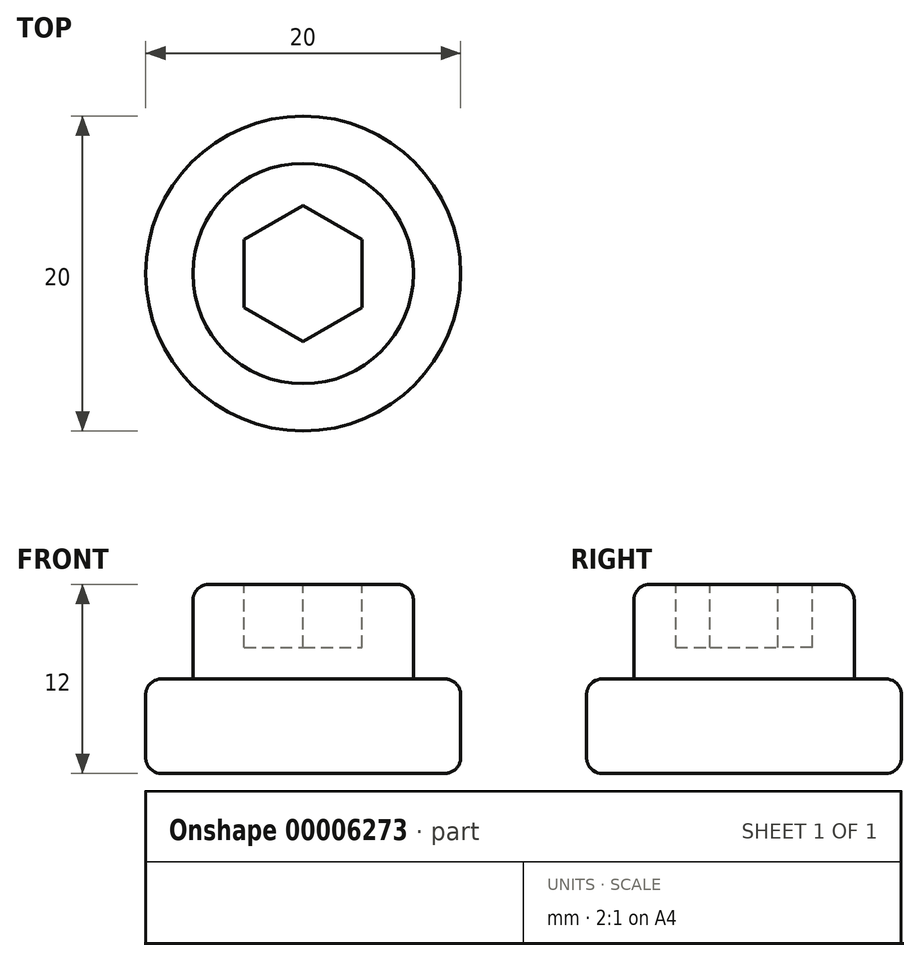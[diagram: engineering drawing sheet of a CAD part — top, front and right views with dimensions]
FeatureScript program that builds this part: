
annotation { "Feature Type Name" : "Feature", "Feature Type Description" : "" }
export const myFeature = defineFeature(function(context is Context, id is Id, definition is map)
    precondition{}
    {
        {
            var Q0;
            Q0=qCreatedBy(makeId("Top.planeOp"),FACE);
            var sketch = newSketch(context, id + "F0", { "sketchPlane" : qUnion([Q0])});
            skCircle(sketch, "E0", {"center": v(0, 0) * mm, "radius": 10 * mm});
            skSolve(sketch);
        }
        {
            var Q0;
            Q0 = qSketchRegion(id + "F0", true);
            extrude(context, id + "F1", {"entities" : qUnion([Q0]), "depth" : 6 * mm});
        }
        {
            var Q0;
            Q0=makeQuery(id+"F1.opExtrude","CAP_FACE",FACE,{"disambiguationData":[OSD([sQuery(id+"F0.wireOp",EDGE,"E0")])],"isStart":false});
            var sketch = newSketch(context, id + "F2", { "sketchPlane" : qUnion([Q0])});
            skCircle(sketch, "E1", {"center": v(0, 0) * mm, "radius": 7 * mm});
            skSolve(sketch);
        }
        {
            var Q0;
            Q0 = qSketchRegion(id + "F2", true);
            extrude(context, id + "F3", {"entities" : qUnion([Q0]), "operationType" : NewBodyOperationType.ADD, "depth" : 6 * mm});
        }
        {
            var Q0;
            Q0=makeQuery(id+"F3.opExtrude","CAP_FACE",FACE,{"disambiguationData":[OSD([sQuery(id+"F2.wireOp",EDGE,"E1")])],"isStart":false});
            var sketch = newSketch(context, id + "F4", { "sketchPlane" : qUnion([Q0])});
            skCircle(sketch, "E2.cCircle", {"center": v(0, 0) * mm, "radius": 3.75 * mm, "construction": true});
            skLineSegment(sketch, "E2.0", {"start": v(0, 4.33) * mm, "end": v(3.75, 2.17) * mm});
            skLineSegment(sketch, "E2.1", {"start": v(3.75, 2.17) * mm, "end": v(3.75, -2.17) * mm});
            skLineSegment(sketch, "E2.2", {"start": v(3.75, -2.17) * mm, "end": v(0, -4.33) * mm});
            skLineSegment(sketch, "E2.3", {"start": v(0, -4.33) * mm, "end": v(-3.75, -2.17) * mm});
            skLineSegment(sketch, "E2.4", {"start": v(-3.75, -2.17) * mm, "end": v(-3.75, 2.17) * mm});
            skLineSegment(sketch, "E2.5", {"start": v(-3.75, 2.17) * mm, "end": v(0, 4.33) * mm});
            skPoint(sketch, "E2.0.midPoint", {"position": v(1.88, 3.25) * mm});
            skSolve(sketch);
        }
        {
            var Q0;
            Q0 = qSketchRegion(id + "F4", true);
            extrude(context, id + "F5", {"entities" : qUnion([Q0]), "operationType" : NewBodyOperationType.REMOVE, "oppositeDirection" : true, "depth" : 4 * mm});
        }
        {
            var Q0;
            Q0=makeQuery(id+"F3.opExtrude","CAP_EDGE",EDGE,{"disambiguationData":[OSD([sQuery(id+"F2.wireOp",EDGE,"E1")])],"isStart":false});
            var Q1;
            Q1=makeQuery(id+"F3.opExtrude","CAP_EDGE",EDGE,{"disambiguationData":[OSD([sQuery(id+"F2.wireOp",EDGE,"E1")])],"isStart":true});
            var Q2;
            Q2=makeQuery(id+"F1.opExtrude","CAP_EDGE",EDGE,{"disambiguationData":[OSD([sQuery(id+"F0.wireOp",EDGE,"E0")])],"isStart":false});
            var Q3;
            Q3=makeQuery(id+"F1.opExtrude","CAP_EDGE",EDGE,{"disambiguationData":[OSD([sQuery(id+"F0.wireOp",EDGE,"E0")])],"isStart":true});
            fillet(context, id + "F6", {"entities" : qUnion([Q0, Q1, Q2, Q3]), "radius" : 1 * mm, "tangentPropagation" : true, "allowEdgeOverflow" : false});
        }
    });
